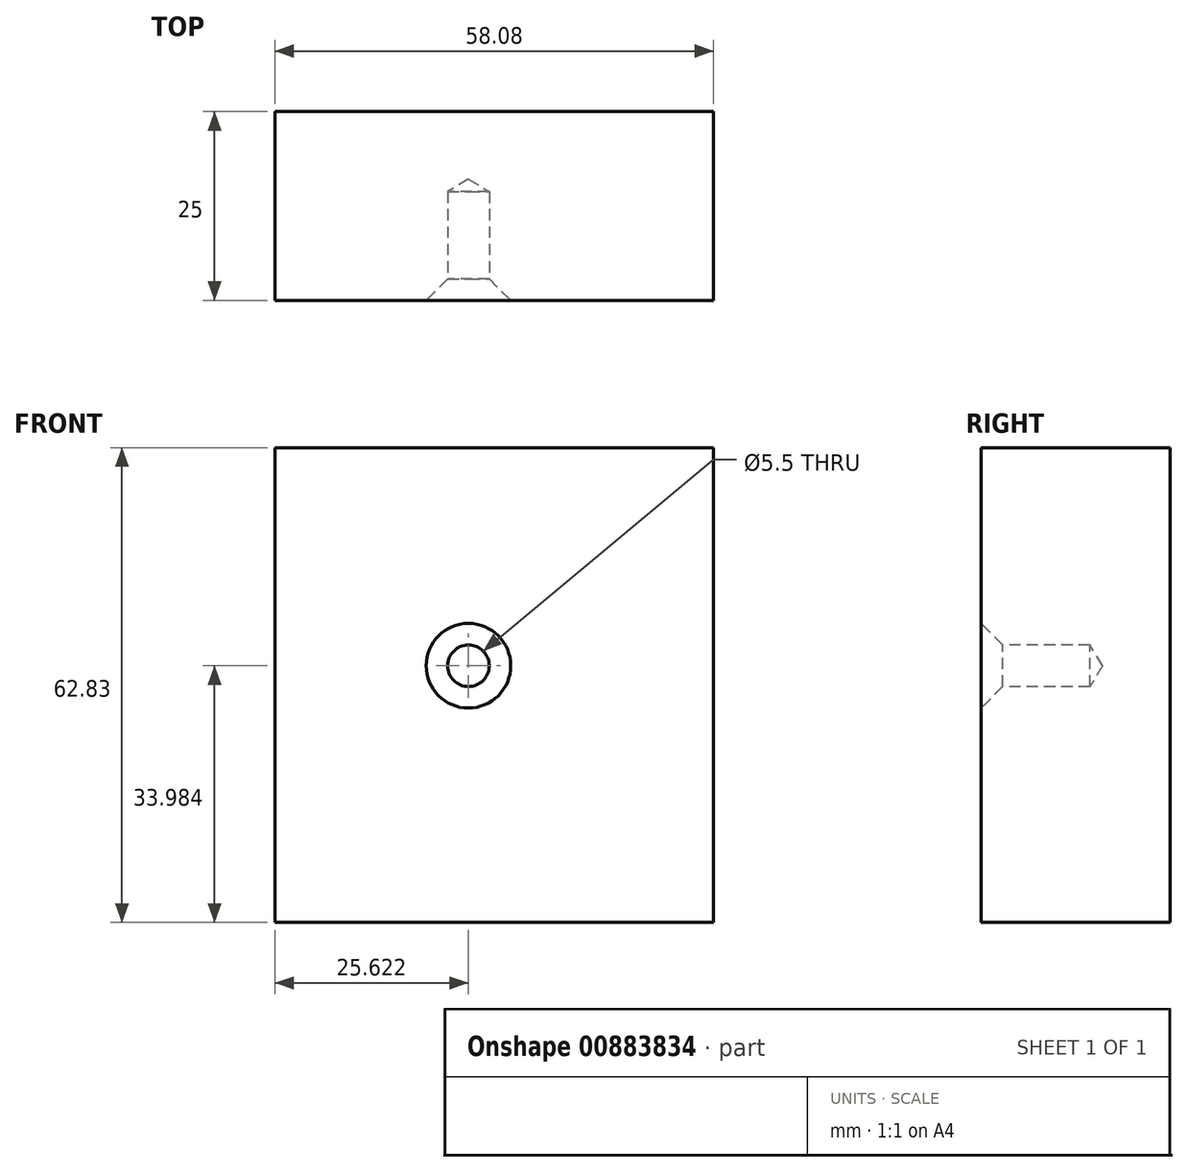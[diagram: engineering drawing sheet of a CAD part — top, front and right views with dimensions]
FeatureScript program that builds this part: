
annotation { "Feature Type Name" : "Feature", "Feature Type Description" : "" }
export const myFeature = defineFeature(function(context is Context, id is Id, definition is map)
    precondition{}
    {
        {
            var Q0;
            Q0=qCreatedBy(makeId("Front.planeOp"),FACE);
            var sketch = newSketch(context, id + "F0", { "sketchPlane" : qUnion([Q0])});
            skLineSegment(sketch, "E0.bottom", {"start": v(-117.33, -12) * mm, "end": v(-59.25, -12) * mm});
            skLineSegment(sketch, "E0.top", {"start": v(-117.33, 50.82) * mm, "end": v(-59.25, 50.82) * mm});
            skLineSegment(sketch, "E0.left", {"start": v(-117.33, -12) * mm, "end": v(-117.33, 50.82) * mm});
            skLineSegment(sketch, "E0.right", {"start": v(-59.25, -12) * mm, "end": v(-59.25, 50.82) * mm});
            skPoint(sketch, "E0.middle", {"position": v(-88.29, 19.4) * mm});
            skSolve(sketch);
        }
        {
            var Q0;
            Q0=makeQuery(id+"F0.imprint","IMPRINT",FACE,{"disambiguationData":[TD([[makeQuery(id+"F0.imprint","IMPRINT",EDGE,{"derivedFrom":sQuery(id+"F0.wireOp",EDGE,"E0.bottom")}),1.0]])]});
            extrude(context, id + "F1", {"entities" : qUnion([Q0]), "depth" : 25 * mm, "offsetDistance" : 25 * mm});
        }
        {
            var Q0;
            Q0=makeQuery(id+"F1.opExtrude","CAP_FACE",FACE,{"disambiguationData":[OSD([sQuery(id+"F0.wireOp",EDGE,"E0.bottom"),sQuery(id+"F0.wireOp",EDGE,"E0.top"),sQuery(id+"F0.wireOp",EDGE,"E0.left"),sQuery(id+"F0.wireOp",EDGE,"E0.right")])],"isStart":false});
            var sketch = newSketch(context, id + "F2", { "sketchPlane" : qUnion([Q0])});
            skPoint(sketch, "E1", {"position": v(-91.7, 21.97) * mm});
            skSolve(sketch);
        }
        {
            var Q0;
            Q0=sQuery(id+"F2.wireOp",VERTEX,"E1");
            var Q1;
            Q1=makeQuery(id+"F1.opExtrude","SWEPT_BODY",BODY,{"disambiguationData":[OSD([sQuery(id+"F0.wireOp",EDGE,"E0.bottom"),sQuery(id+"F0.wireOp",EDGE,"E0.top"),sQuery(id+"F0.wireOp",EDGE,"E0.left"),sQuery(id+"F0.wireOp",EDGE,"E0.right")])]});
            hole(context, id + "F3", {"style" : HoleStyle.C_SINK, "endStyle" : HoleEndStyle.BLIND, "standardTappedOrClearance" : lookupTablePath({ "fit" : "Normal", "standard" : "ISO", "size" : "M5", "type" : "Clearance" }), "standardBlindInLast" : lookupTablePath({ "fit" : "Normal", "standard" : "ISO", "size" : "M5", "type" : "Clearance" }), "holeDiameter" : 5.5 * mm, "cSinkDiameter" : 11.2 * mm, "cSinkAngle" : 90 * degree, "majorDiameter" : 5 * mm, "holeDepth" : 14.4 * mm, "isTappedThrough" : true, "tappedDepth" : 12 * mm, "tapClearance" : 3, "locations" : qUnion([Q0]), "scope" : qUnion([Q1])});
        }
    });
